# Revit family: 2Incepa_Bali_Coluna Suspensa para Lavatório_25202
name_source: partatom
category: Plumbing Fixtures
revit_build: Autodesk Revit MEP 2014 (Build: 20131024_2115(x64)
units: mm (PartAtom-declared; Revit-internal decimal feet)

## types (2) — shared parameters
Assembly Code = D2010400
Desenvolvido por = ofcdesk
Incepa: Categoria = Linhas Completas
Incepa: Código = 25202
Incepa: Desenho Técnico = http://www.banheirosincepa.com.br
Incepa: Fabricante = Incepa
Incepa: Linha = Bali
Incepa: Link do Produto = http://www.banheirosincepa.com.br
Incepa: Norma = ABNT NBR 15097-1: 2011 - Requisitos e métodos de ensaio
Incepa: Produto = Colunas
Incepa: Tipo = Colunas para lavatórios
Incepa: Versão = Autodesk Revit MEP 2014
Manufacturer = Incepa
Model = 25202
Selo de Qualidade ofcdesk = Standard
URL = http://www.banheirosincepa.com.br
zero-valued in all types: CWFU, Default Elevation, HWFU, WFU

## per-type parameters (varying)
| type | Description | Incepa: Cores Disponíveis | Incepa: Descrição |
| 01 - Branco | Coluna suspensa para lavatório cor branca (25202), linha Bali - Louças Incepa | Branco | Coluna suspensa para lavatório cor branca (25202), linha Bali - Louças Incepa |
| 57 - Biscuit | Coluna suspensa para lavatório cor biscuit (25202), linha Bali - Louças Incepa | Biscuit | Coluna suspensa para lavatório cor biscuit (25202), linha Bali - Louças Incepa |

## geometry (parser evidence)
native form markers: Sweep x3
no freeform markers — native parametric forms only
